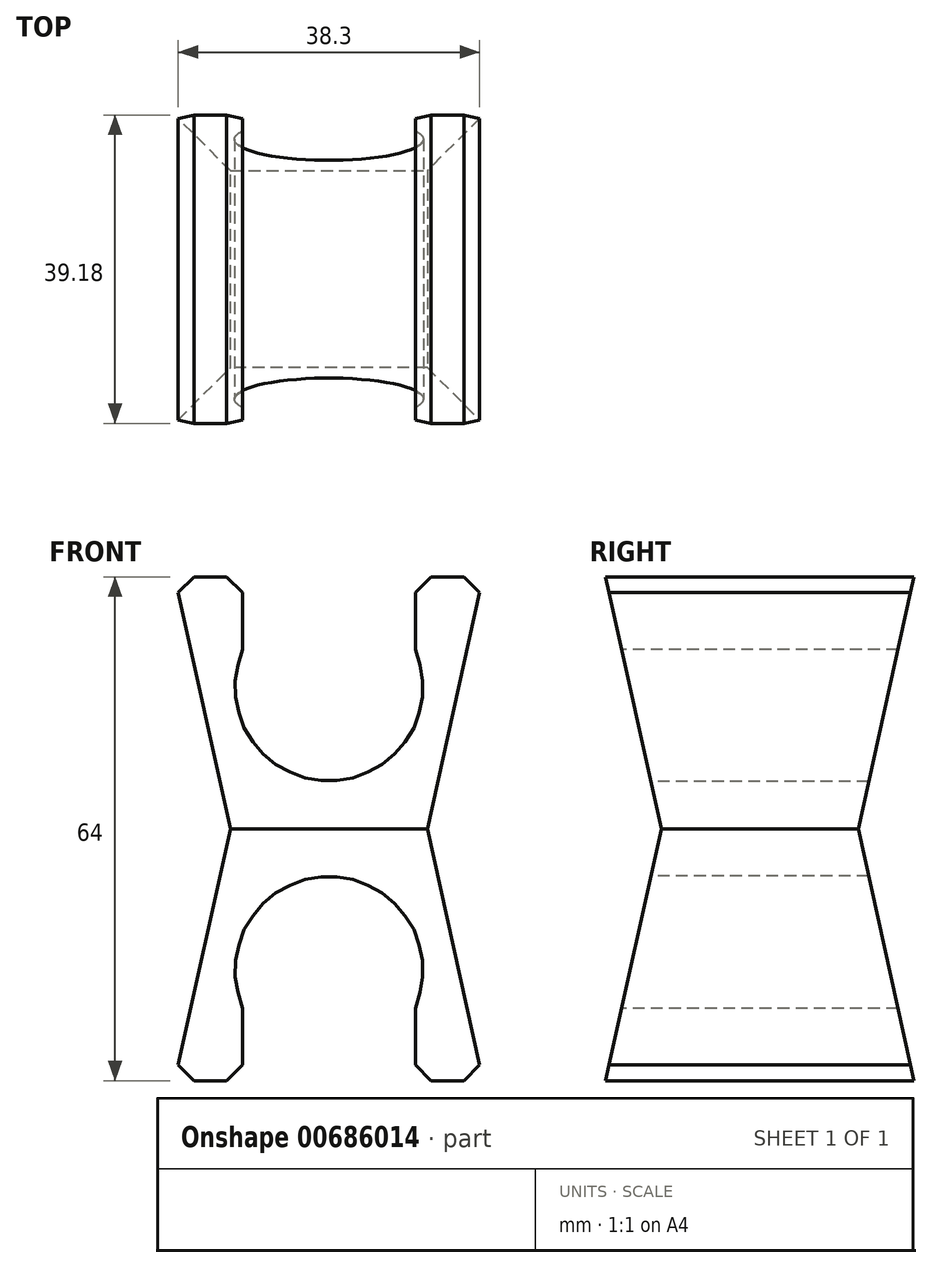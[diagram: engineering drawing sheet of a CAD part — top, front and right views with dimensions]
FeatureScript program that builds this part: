
annotation { "Feature Type Name" : "Feature", "Feature Type Description" : "" }
export const myFeature = defineFeature(function(context is Context, id is Id, definition is map)
    precondition{}
    {
        {
            var Q0;
            Q0=qCreatedBy(makeId("Top.planeOp"),FACE);
            var sketch = newSketch(context, id + "F0", { "sketchPlane" : qUnion([Q0])});
            skLineSegment(sketch, "E0.bottom", {"start": v(-12.5, 12.5) * mm, "end": v(12.5, 12.5) * mm});
            skLineSegment(sketch, "E0.top", {"start": v(-12.5, -12.5) * mm, "end": v(12.5, -12.5) * mm});
            skLineSegment(sketch, "E0.left", {"start": v(-12.5, 12.5) * mm, "end": v(-12.5, -12.5) * mm});
            skLineSegment(sketch, "E0.right", {"start": v(12.5, 12.5) * mm, "end": v(12.5, -12.5) * mm});
            skPoint(sketch, "E0.middle", {"position": v(0, 0) * mm});
            skSolve(sketch);
        }
        {
            var Q0;
            Q0=makeQuery(id+"F0.imprint","IMPRINT",FACE,{"disambiguationData":[TD([[makeQuery(id+"F0.imprint","IMPRINT",EDGE,{"derivedFrom":sQuery(id+"F0.wireOp",EDGE,"E0.bottom")}),-1.0]])]});
            extrude(context, id + "F1", {"entities" : qUnion([Q0]), "depth" : 32 * mm, "offsetDistance" : 25 * mm, "hasDraft" : true, "draftAngle" : 12.5 * degree});
        }
        {
            var Q0;
            Q0=qCreatedBy(makeId("Front.planeOp"),FACE);
            var sketch = newSketch(context, id + "F2", { "sketchPlane" : qUnion([Q0])});
            skCircle(sketch, "E1", {"center": v(0, 18) * mm, "radius": 12 * mm});
            skLineSegment(sketch, "E2", {"start": v(-11, 22.8) * mm, "end": v(11, 22.8) * mm, "construction": true});
            skLineSegment(sketch, "E3", {"start": v(-11, 22.8) * mm, "end": v(-11, 30) * mm});
            skLineSegment(sketch, "E4", {"start": v(-11, 30) * mm, "end": v(-13, 32) * mm});
            skLineSegment(sketch, "E5", {"start": v(-13, 32) * mm, "end": v(13, 32) * mm});
            skLineSegment(sketch, "E6", {"start": v(13, 32) * mm, "end": v(11, 30) * mm});
            skLineSegment(sketch, "E7", {"start": v(11, 30) * mm, "end": v(11, 22.8) * mm});
            skLineSegment(sketch, "E8", {"start": v(-17.15, 32) * mm, "end": v(-19.15, 30) * mm});
            skLineSegment(sketch, "E9", {"start": v(-19.15, 30) * mm, "end": v(-19.6, 32) * mm});
            skLineSegment(sketch, "E10", {"start": v(-19.6, 32) * mm, "end": v(-17.15, 32) * mm});
            skLineSegment(sketch, "E11", {"start": v(17.15, 32) * mm, "end": v(19.15, 30) * mm});
            skLineSegment(sketch, "E12", {"start": v(19.15, 30) * mm, "end": v(19.6, 32) * mm});
            skLineSegment(sketch, "E13", {"start": v(19.6, 32) * mm, "end": v(17.15, 32) * mm});
            skLineSegment(sketch, "E14", {"start": v(0, 45.45) * mm, "end": v(0, -22.4) * mm, "construction": true});
            skSolve(sketch);
        }
        {
            var Q0;
            {var subQ0=sQuery(id+"F2.wireOp",EDGE,"E3");Q0=makeQuery(id+"F2.imprint","IMPRINT",FACE,{"disambiguationData":[TD([[makeQuery(id+"F2.imprint","IMPRINT",EDGE,{"derivedFrom":subQ0}),-1.0]])]});}
            var Q1;
            {var subQ0=sQuery(id+"F2.wireOp",EDGE,"E1");var subQ1=makeQuery(id+"F2.imprint","INTERSECT",VERTEX,{"derivedFrom":[subQ0,sQuery(id+"F2.wireOp",EDGE,"E3")]});Q1=makeQuery(id+"F2.imprint","IMPRINT",FACE,{"disambiguationData":[TD([[makeQuery(id+"F2.imprint","IMPRINT",EDGE,{"disambiguationData":[TD([[subQ1,1.0]])],"derivedFrom":subQ0}),1.0]])]});}
            var Q2;
            Q2=makeQuery(id+"F2.imprint","IMPRINT",FACE,{"disambiguationData":[TD([[makeQuery(id+"F2.imprint","IMPRINT",EDGE,{"derivedFrom":sQuery(id+"F2.wireOp",EDGE,"E8")}),-1.0]])]});
            var Q3;
            Q3=makeQuery(id+"F2.imprint","IMPRINT",FACE,{"disambiguationData":[TD([[makeQuery(id+"F2.imprint","IMPRINT",EDGE,{"derivedFrom":sQuery(id+"F2.wireOp",EDGE,"E11")}),1.0]])]});
            extrude(context, id + "F3", {"entities" : qUnion([Q0, Q1, Q2, Q3]), "operationType" : NewBodyOperationType.REMOVE, "oppositeDirection" : true, "depth" : 50 * mm, "offsetDistance" : 25 * mm, "symmetric" : true});
        }
        {
            var Q0;
            Q0=makeQuery(id+"F1.opExtrude","SWEPT_BODY",BODY,{"disambiguationData":[OSD([sQuery(id+"F0.wireOp",EDGE,"E0.bottom"),sQuery(id+"F0.wireOp",EDGE,"E0.top"),sQuery(id+"F0.wireOp",EDGE,"E0.left"),sQuery(id+"F0.wireOp",EDGE,"E0.right")])]});
            var Q1;
            Q1=qCreatedBy(makeId("Top.planeOp"),FACE);
            mirror(context, id + "F4", {"operationType" : NewBodyOperationType.ADD, "entities" : qUnion([Q0]), "mirrorPlane" : qUnion([Q1])});
        }
    });
